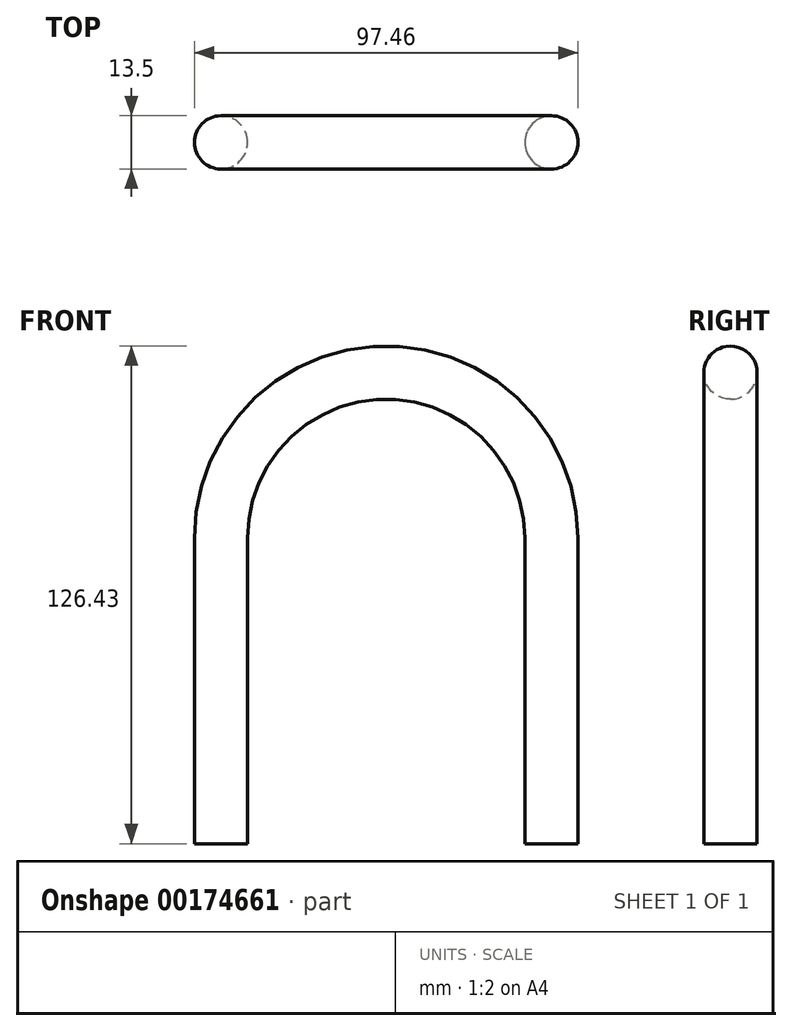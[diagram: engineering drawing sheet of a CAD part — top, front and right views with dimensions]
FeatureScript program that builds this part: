
annotation { "Feature Type Name" : "Feature", "Feature Type Description" : "" }
export const myFeature = defineFeature(function(context is Context, id is Id, definition is map)
    precondition{}
    {
        {
            var Q0;
            Q0=qCreatedBy(makeId("Front.planeOp"),FACE);
            var sketch = newSketch(context, id + "F0", { "sketchPlane" : qUnion([Q0])});
            skArc(sketch, "E0", {"start": v(41.97, 22.74) * mm, "mid": v(0, 64.7) * mm, "end": v(-41.97, 22.74) * mm});
            skLineSegment(sketch, "E1", {"start": v(-41.97, 22.74) * mm, "end": v(-41.97, -54.97) * mm});
            skLineSegment(sketch, "E2", {"start": v(41.97, 22.74) * mm, "end": v(41.97, -54.97) * mm});
            skSolve(sketch);
        }
        {
            var Q0;
            Q0=qCreatedBy(makeId("Top.planeOp"),FACE);
            var Q1;
            Q1=sQuery(id+"F0.wireOp",VERTEX,"E1.end");
            cPlane(context, id + "F1", {"entities" : qUnion([Q0, Q1]), "cplaneType" : CPlaneType.PLANE_POINT, "offset" : 25.4 * mm, "width" : 152.4 * mm, "height" : 152.4 * mm});
        }
        {
            var Q0;
            Q0=qCreatedBy(id+"F1.planeOp",FACE);
            var sketch = newSketch(context, id + "F2", { "sketchPlane" : qUnion([Q0])});
            skCircle(sketch, "E3", {"center": v(-41.97, 0) * mm, "radius": 6.75 * mm});
            skSolve(sketch);
        }
        {
            var Q0;
            Q0=makeQuery(id+"F2.imprint","IMPRINT",FACE,{"disambiguationData":[TD([[makeQuery(id+"F2.imprint","IMPRINT",EDGE,{"derivedFrom":sQuery(id+"F2.wireOp",EDGE,"E3")}),1.0]])]});
            var Q1;
            Q1=sQuery(id+"F0.wireOp",EDGE,"E1");
            var Q2;
            Q2=sQuery(id+"F0.wireOp",EDGE,"E0");
            var Q3;
            Q3=sQuery(id+"F0.wireOp",EDGE,"E2");
            sweep(context, id + "F3", {"profiles" : qUnion([Q0]), "path" : qUnion([Q1, Q2, Q3])});
        }
    });
